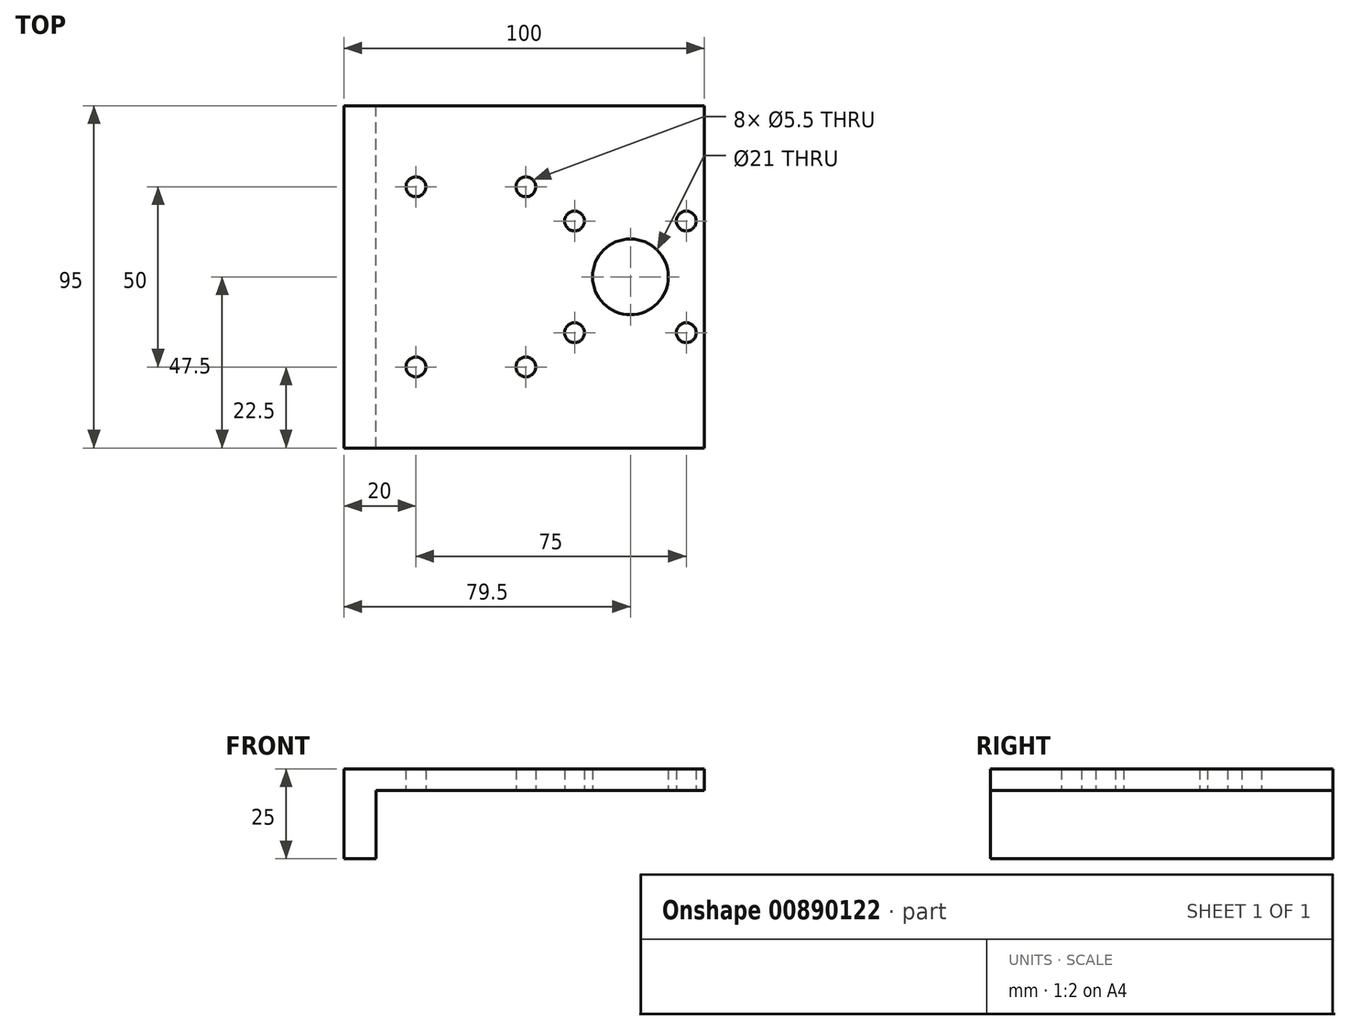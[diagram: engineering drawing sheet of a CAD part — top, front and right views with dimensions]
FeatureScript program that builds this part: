
annotation { "Feature Type Name" : "Feature", "Feature Type Description" : "" }
export const myFeature = defineFeature(function(context is Context, id is Id, definition is map)
    precondition{}
    {
        {
            var Q0;
            Q0=qCreatedBy(makeId("Front.planeOp"),FACE);
            var sketch = newSketch(context, id + "F0", { "sketchPlane" : qUnion([Q0])});
            skLineSegment(sketch, "E0", {"start": v(0, 0) * mm, "end": v(-100, 0) * mm});
            skLineSegment(sketch, "E1", {"start": v(-100, 0) * mm, "end": v(-100, -25) * mm});
            skLineSegment(sketch, "E2", {"start": v(-100, -25) * mm, "end": v(-91, -25) * mm});
            skLineSegment(sketch, "E3", {"start": v(-91, -25) * mm, "end": v(-91, -6) * mm});
            skLineSegment(sketch, "E4", {"start": v(-91, -6) * mm, "end": v(0, -6) * mm});
            skLineSegment(sketch, "E5", {"start": v(0, -6) * mm, "end": v(0, 0) * mm});
            skSolve(sketch);
        }
        {
            var Q0;
            Q0=qSketchRegion(id+"F0",true);
            extrude(context, id + "F1", {"entities" : qUnion([Q0]), "depth" : 95 * mm, "offsetDistance" : 25 * mm});
        }
        {
            var Q0;
            Q0=makeQuery(id+"F1.opExtrude","SWEPT_FACE",FACE,{"disambiguationData":[OSD([sQuery(id+"F0.wireOp",EDGE,"E4")])]});
            var sketch = newSketch(context, id + "F2", { "sketchPlane" : qUnion([Q0])});
            skCircle(sketch, "E6", {"center": v(-80, 72.5) * mm, "radius": 2.75 * mm});
            skCircle(sketch, "E7", {"center": v(-49.5, 72.5) * mm, "radius": 2.75 * mm});
            skCircle(sketch, "E8", {"center": v(-80, 22.5) * mm, "radius": 2.75 * mm});
            skCircle(sketch, "E9", {"center": v(-49.5, 22.5) * mm, "radius": 2.75 * mm});
            skCircle(sketch, "E10", {"center": v(-5, 32) * mm, "radius": 2.75 * mm});
            skCircle(sketch, "E11", {"center": v(-5, 63) * mm, "radius": 2.75 * mm});
            skCircle(sketch, "E12", {"center": v(-36, 32) * mm, "radius": 2.75 * mm});
            skCircle(sketch, "E13", {"center": v(-36, 63) * mm, "radius": 2.75 * mm});
            skCircle(sketch, "E14", {"center": v(-20.5, 47.5) * mm, "radius": 10.5 * mm});
            skLineSegment(sketch, "E15", {"start": v(-5, 32) * mm, "end": v(-36, 63) * mm, "construction": true});
            skLineSegment(sketch, "E16", {"start": v(-36, 32) * mm, "end": v(-5, 63) * mm, "construction": true});
            skLineSegment(sketch, "E17", {"start": v(-42, 66.95) * mm, "end": v(-42, 36.97) * mm, "construction": true});
            skSolve(sketch);
        }
        {
            var Q0;
            Q0=qSketchRegion(id+"F2",true);
            extrude(context, id + "F3", {"entities" : qUnion([Q0]), "operationType" : NewBodyOperationType.REMOVE, "oppositeDirection" : true, "depth" : 6 * mm, "offsetDistance" : 25 * mm});
        }
    });
